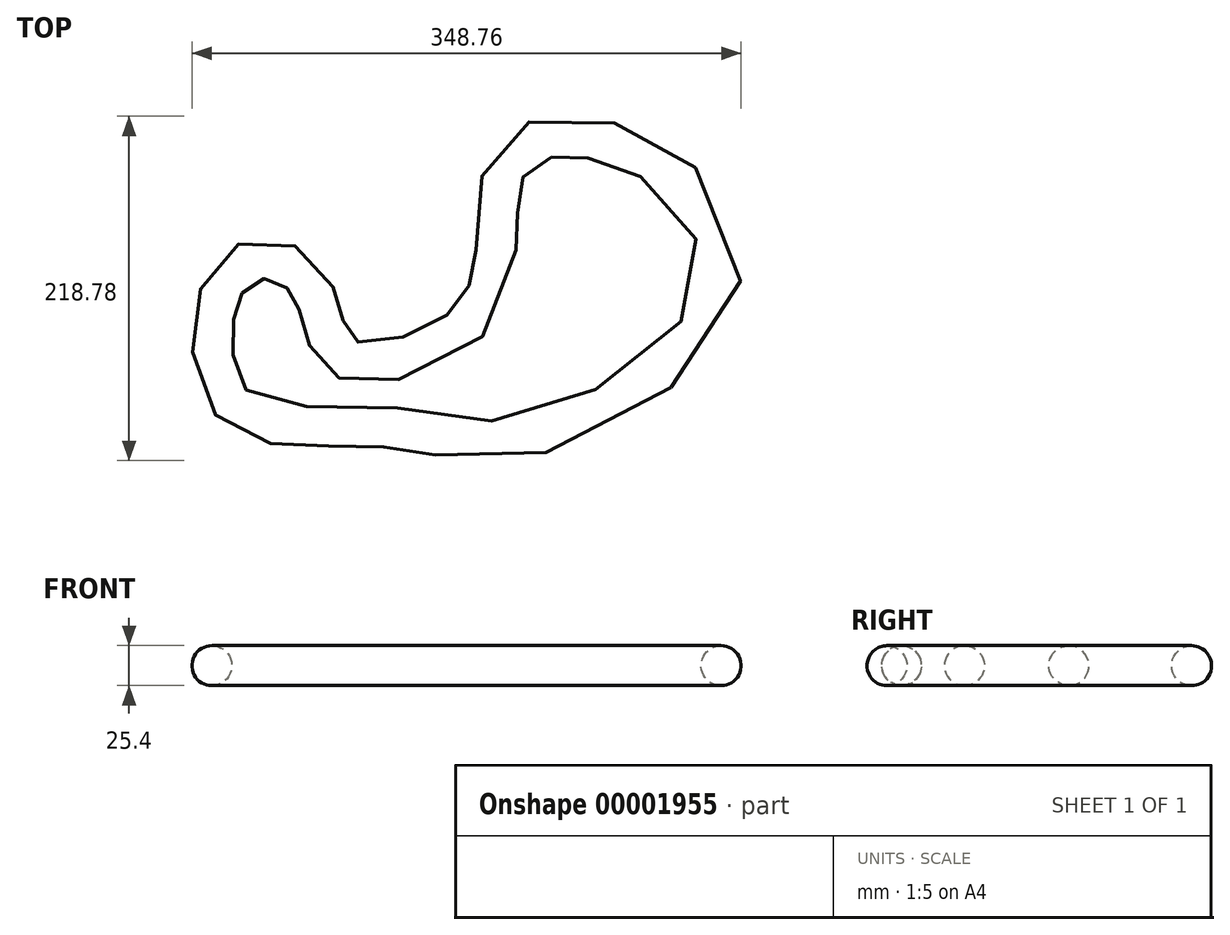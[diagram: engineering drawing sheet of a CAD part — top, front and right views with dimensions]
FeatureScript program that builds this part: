
annotation { "Feature Type Name" : "Feature", "Feature Type Description" : "" }
export const myFeature = defineFeature(function(context is Context, id is Id, definition is map)
    precondition{}
    {
        {
            var Q0;
            Q0=qCreatedBy(makeId("Front.planeOp"),FACE);
            var sketch = newSketch(context, id + "F0", { "sketchPlane" : qUnion([Q0])});
            skCircle(sketch, "E0", {"center": v(0, 0) * mm, "radius": 12.7 * mm});
            skSolve(sketch);
        }
        {
            var Q0;
            Q0=qCreatedBy(makeId("Top.planeOp"),FACE);
            var sketch = newSketch(context, id + "F1", { "sketchPlane" : qUnion([Q0])});
            skFitSpline(sketch, "E1", {"points": [v(0, 0) * mm, v(-25.05, -52.3) * mm, v(-98.73, -67.4) * mm, v(-119.93, -19.44) * mm, v(-165.25, -12.02) * mm, v(-168.7, -96.56) * mm, v(-75.93, -111.94) * mm, v(14.7, -119.36) * mm, v(138.75, -32.95) * mm, v(103.76, 54.25) * mm, v(13.65, 63.26) * mm, v(0, 0) * mm]});
            skPoint(sketch, "E2", {"position": v(3.66, 45.6) * mm});
            skPoint(sketch, "E3", {"position": v(0.4, 8.33) * mm});
            skSolve(sketch);
        }
        {
            var Q0;
            Q0 = qSketchRegion(id + "F0", true);
            var Q1;
            Q1=sQuery(id+"F1.wireOp",EDGE,"E1");
            sweep(context, id + "F2", {"profiles" : qUnion([Q0]), "path" : qUnion([Q1])});
        }
    });
